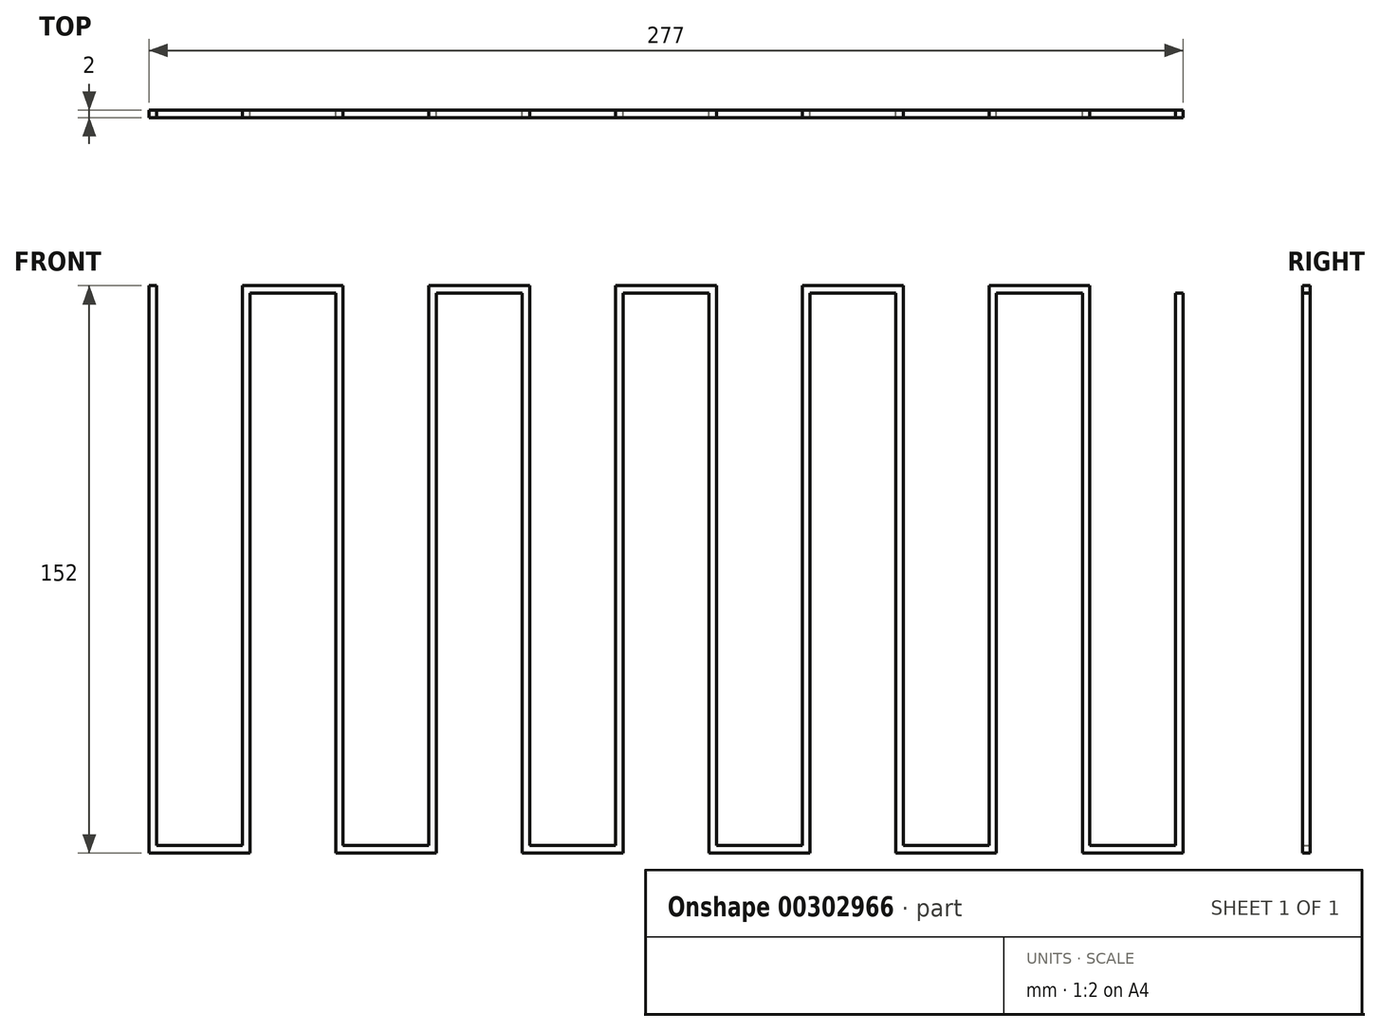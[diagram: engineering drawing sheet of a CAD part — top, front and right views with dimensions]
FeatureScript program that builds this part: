
annotation { "Feature Type Name" : "Feature", "Feature Type Description" : "" }
export const myFeature = defineFeature(function(context is Context, id is Id, definition is map)
    precondition{}
    {
        {
            var Q0;
            Q0=qCreatedBy(makeId("Front.planeOp"),FACE);
            var sketch = newSketch(context, id + "F0", { "sketchPlane" : qUnion([Q0])});
            skLineSegment(sketch, "E0.bottom", {"start": v(-47.26, 125.58) * mm, "end": v(-45.26, 125.58) * mm});
            skLineSegment(sketch, "E0.top", {"start": v(-47.26, -24.42) * mm, "end": v(-45.26, -24.42) * mm});
            skLineSegment(sketch, "E0.left", {"start": v(-47.26, 125.58) * mm, "end": v(-47.26, -24.42) * mm});
            skLineSegment(sketch, "E0.right", {"start": v(-45.26, 125.58) * mm, "end": v(-45.26, -24.42) * mm});
            skLineSegment(sketch, "E1.bottom", {"start": v(-47.26, -24.42) * mm, "end": v(-22.26, -24.42) * mm});
            skLineSegment(sketch, "E1.top", {"start": v(-47.26, -26.42) * mm, "end": v(-22.26, -26.42) * mm});
            skLineSegment(sketch, "E1.left", {"start": v(-47.26, -24.42) * mm, "end": v(-47.26, -26.42) * mm});
            skLineSegment(sketch, "E1.right", {"start": v(-22.26, -24.42) * mm, "end": v(-22.26, -26.42) * mm});
            skLineSegment(sketch, "E2.bottom", {"start": v(-22.26, -26.42) * mm, "end": v(-20.26, -26.42) * mm});
            skLineSegment(sketch, "E2.top", {"start": v(-22.26, 123.58) * mm, "end": v(-20.26, 123.58) * mm});
            skLineSegment(sketch, "E2.left", {"start": v(-22.26, -26.42) * mm, "end": v(-22.26, 123.58) * mm});
            skLineSegment(sketch, "E2.right", {"start": v(-20.26, -26.42) * mm, "end": v(-20.26, 123.58) * mm});
            skLineSegment(sketch, "E3.bottom", {"start": v(-22.26, 123.58) * mm, "end": v(2.74, 123.58) * mm});
            skLineSegment(sketch, "E3.top", {"start": v(-22.26, 125.58) * mm, "end": v(2.74, 125.58) * mm});
            skLineSegment(sketch, "E3.left", {"start": v(-22.26, 123.58) * mm, "end": v(-22.26, 125.58) * mm});
            skLineSegment(sketch, "E3.right", {"start": v(2.74, 123.58) * mm, "end": v(2.74, 125.58) * mm});
            skLineSegment(sketch, "E4.1.0.0", {"start": v(4.74, 125.58) * mm, "end": v(4.74, -24.42) * mm});
            skLineSegment(sketch, "E4.1.0.1", {"start": v(2.74, -26.42) * mm, "end": v(27.74, -26.42) * mm});
            skLineSegment(sketch, "E4.1.0.2", {"start": v(2.74, -24.42) * mm, "end": v(27.74, -24.42) * mm});
            skLineSegment(sketch, "E4.1.0.3", {"start": v(29.74, -26.42) * mm, "end": v(29.74, 123.58) * mm});
            skLineSegment(sketch, "E4.1.0.4", {"start": v(27.74, 123.58) * mm, "end": v(52.74, 123.58) * mm});
            skLineSegment(sketch, "E4.1.0.5", {"start": v(27.74, -26.42) * mm, "end": v(27.74, 123.58) * mm});
            skLineSegment(sketch, "E4.1.0.6", {"start": v(2.74, 125.58) * mm, "end": v(2.74, -24.42) * mm});
            skLineSegment(sketch, "E4.1.0.7", {"start": v(27.74, 125.58) * mm, "end": v(52.74, 125.58) * mm});
            skLineSegment(sketch, "E4.1.0.8", {"start": v(2.74, 125.58) * mm, "end": v(4.74, 125.58) * mm});
            skLineSegment(sketch, "E4.1.0.9", {"start": v(2.74, -24.42) * mm, "end": v(2.74, -26.42) * mm});
            skLineSegment(sketch, "E4.1.0.10", {"start": v(27.74, -24.42) * mm, "end": v(27.74, -26.42) * mm});
            skLineSegment(sketch, "E4.1.0.11", {"start": v(52.74, 123.58) * mm, "end": v(52.74, 125.58) * mm});
            skLineSegment(sketch, "E4.1.0.12", {"start": v(2.74, -24.42) * mm, "end": v(4.74, -24.42) * mm});
            skLineSegment(sketch, "E4.1.0.13", {"start": v(27.74, -26.42) * mm, "end": v(29.74, -26.42) * mm});
            skLineSegment(sketch, "E4.1.0.14", {"start": v(27.74, 123.58) * mm, "end": v(29.74, 123.58) * mm});
            skLineSegment(sketch, "E4.1.0.15", {"start": v(27.74, 123.58) * mm, "end": v(27.74, 125.58) * mm});
            skLineSegment(sketch, "E4.2.0.0", {"start": v(54.74, 125.58) * mm, "end": v(54.74, -24.42) * mm});
            skLineSegment(sketch, "E4.2.0.1", {"start": v(52.74, -26.42) * mm, "end": v(77.74, -26.42) * mm});
            skLineSegment(sketch, "E4.2.0.2", {"start": v(52.74, -24.42) * mm, "end": v(77.74, -24.42) * mm});
            skLineSegment(sketch, "E4.2.0.3", {"start": v(79.74, -26.42) * mm, "end": v(79.74, 123.58) * mm});
            skLineSegment(sketch, "E4.2.0.4", {"start": v(77.74, 123.58) * mm, "end": v(102.74, 123.58) * mm});
            skLineSegment(sketch, "E4.2.0.5", {"start": v(77.74, -26.42) * mm, "end": v(77.74, 123.58) * mm});
            skLineSegment(sketch, "E4.2.0.6", {"start": v(52.74, 125.58) * mm, "end": v(52.74, -24.42) * mm});
            skLineSegment(sketch, "E4.2.0.7", {"start": v(77.74, 125.58) * mm, "end": v(102.74, 125.58) * mm});
            skLineSegment(sketch, "E4.2.0.8", {"start": v(52.74, 125.58) * mm, "end": v(54.74, 125.58) * mm});
            skLineSegment(sketch, "E4.2.0.9", {"start": v(52.74, -24.42) * mm, "end": v(52.74, -26.42) * mm});
            skLineSegment(sketch, "E4.2.0.10", {"start": v(77.74, -24.42) * mm, "end": v(77.74, -26.42) * mm});
            skLineSegment(sketch, "E4.2.0.11", {"start": v(102.74, 123.58) * mm, "end": v(102.74, 125.58) * mm});
            skLineSegment(sketch, "E4.2.0.12", {"start": v(52.74, -24.42) * mm, "end": v(54.74, -24.42) * mm});
            skLineSegment(sketch, "E4.2.0.13", {"start": v(77.74, -26.42) * mm, "end": v(79.74, -26.42) * mm});
            skLineSegment(sketch, "E4.2.0.14", {"start": v(77.74, 123.58) * mm, "end": v(79.74, 123.58) * mm});
            skLineSegment(sketch, "E4.2.0.15", {"start": v(77.74, 123.58) * mm, "end": v(77.74, 125.58) * mm});
            skLineSegment(sketch, "E4.3.0.0", {"start": v(104.74, 125.58) * mm, "end": v(104.74, -24.42) * mm});
            skLineSegment(sketch, "E4.3.0.1", {"start": v(102.74, -26.42) * mm, "end": v(127.74, -26.42) * mm});
            skLineSegment(sketch, "E4.3.0.2", {"start": v(102.74, -24.42) * mm, "end": v(127.74, -24.42) * mm});
            skLineSegment(sketch, "E4.3.0.3", {"start": v(129.74, -26.42) * mm, "end": v(129.74, 123.58) * mm});
            skLineSegment(sketch, "E4.3.0.4", {"start": v(127.74, 123.58) * mm, "end": v(152.74, 123.58) * mm});
            skLineSegment(sketch, "E4.3.0.5", {"start": v(127.74, -26.42) * mm, "end": v(127.74, 123.58) * mm});
            skLineSegment(sketch, "E4.3.0.6", {"start": v(102.74, 125.58) * mm, "end": v(102.74, -24.42) * mm});
            skLineSegment(sketch, "E4.3.0.7", {"start": v(127.74, 125.58) * mm, "end": v(152.74, 125.58) * mm});
            skLineSegment(sketch, "E4.3.0.8", {"start": v(102.74, 125.58) * mm, "end": v(104.74, 125.58) * mm});
            skLineSegment(sketch, "E4.3.0.9", {"start": v(102.74, -24.42) * mm, "end": v(102.74, -26.42) * mm});
            skLineSegment(sketch, "E4.3.0.10", {"start": v(127.74, -24.42) * mm, "end": v(127.74, -26.42) * mm});
            skLineSegment(sketch, "E4.3.0.11", {"start": v(152.74, 123.58) * mm, "end": v(152.74, 125.58) * mm});
            skLineSegment(sketch, "E4.3.0.12", {"start": v(102.74, -24.42) * mm, "end": v(104.74, -24.42) * mm});
            skLineSegment(sketch, "E4.3.0.13", {"start": v(127.74, -26.42) * mm, "end": v(129.74, -26.42) * mm});
            skLineSegment(sketch, "E4.3.0.14", {"start": v(127.74, 123.58) * mm, "end": v(129.74, 123.58) * mm});
            skLineSegment(sketch, "E4.3.0.15", {"start": v(127.74, 123.58) * mm, "end": v(127.74, 125.58) * mm});
            skLineSegment(sketch, "E4.4.0.0", {"start": v(154.74, 125.58) * mm, "end": v(154.74, -24.42) * mm});
            skLineSegment(sketch, "E4.4.0.1", {"start": v(152.74, -26.42) * mm, "end": v(177.74, -26.42) * mm});
            skLineSegment(sketch, "E4.4.0.2", {"start": v(152.74, -24.42) * mm, "end": v(177.74, -24.42) * mm});
            skLineSegment(sketch, "E4.4.0.3", {"start": v(179.74, -26.42) * mm, "end": v(179.74, 123.58) * mm});
            skLineSegment(sketch, "E4.4.0.4", {"start": v(177.74, 123.58) * mm, "end": v(202.74, 123.58) * mm});
            skLineSegment(sketch, "E4.4.0.5", {"start": v(177.74, -26.42) * mm, "end": v(177.74, 123.58) * mm});
            skLineSegment(sketch, "E4.4.0.6", {"start": v(152.74, 125.58) * mm, "end": v(152.74, -24.42) * mm});
            skLineSegment(sketch, "E4.4.0.7", {"start": v(177.74, 125.58) * mm, "end": v(202.74, 125.58) * mm});
            skLineSegment(sketch, "E4.4.0.8", {"start": v(152.74, 125.58) * mm, "end": v(154.74, 125.58) * mm});
            skLineSegment(sketch, "E4.4.0.9", {"start": v(152.74, -24.42) * mm, "end": v(152.74, -26.42) * mm});
            skLineSegment(sketch, "E4.4.0.10", {"start": v(177.74, -24.42) * mm, "end": v(177.74, -26.42) * mm});
            skLineSegment(sketch, "E4.4.0.11", {"start": v(202.74, 123.58) * mm, "end": v(202.74, 125.58) * mm});
            skLineSegment(sketch, "E4.4.0.12", {"start": v(152.74, -24.42) * mm, "end": v(154.74, -24.42) * mm});
            skLineSegment(sketch, "E4.4.0.13", {"start": v(177.74, -26.42) * mm, "end": v(179.74, -26.42) * mm});
            skLineSegment(sketch, "E4.4.0.14", {"start": v(177.74, 123.58) * mm, "end": v(179.74, 123.58) * mm});
            skLineSegment(sketch, "E4.4.0.15", {"start": v(177.74, 123.58) * mm, "end": v(177.74, 125.58) * mm});
            skLineSegment(sketch, "E4.5.0.0", {"start": v(204.74, 125.58) * mm, "end": v(204.74, -24.42) * mm});
            skLineSegment(sketch, "E4.5.0.1", {"start": v(202.74, -26.42) * mm, "end": v(227.74, -26.42) * mm});
            skLineSegment(sketch, "E4.5.0.2", {"start": v(202.74, -24.42) * mm, "end": v(227.74, -24.42) * mm});
            skLineSegment(sketch, "E4.5.0.3", {"start": v(229.74, -26.42) * mm, "end": v(229.74, 123.58) * mm});
            skLineSegment(sketch, "E4.5.0.5", {"start": v(227.74, -26.42) * mm, "end": v(227.74, 123.58) * mm});
            skLineSegment(sketch, "E4.5.0.6", {"start": v(202.74, 125.58) * mm, "end": v(202.74, -24.42) * mm});
            skLineSegment(sketch, "E4.5.0.8", {"start": v(202.74, 125.58) * mm, "end": v(204.74, 125.58) * mm});
            skLineSegment(sketch, "E4.5.0.9", {"start": v(202.74, -24.42) * mm, "end": v(202.74, -26.42) * mm});
            skLineSegment(sketch, "E4.5.0.10", {"start": v(227.74, -24.42) * mm, "end": v(227.74, -26.42) * mm});
            skLineSegment(sketch, "E4.5.0.12", {"start": v(202.74, -24.42) * mm, "end": v(204.74, -24.42) * mm});
            skLineSegment(sketch, "E4.5.0.13", {"start": v(227.74, -26.42) * mm, "end": v(229.74, -26.42) * mm});
            skLineSegment(sketch, "E4.5.0.14", {"start": v(227.74, 123.58) * mm, "end": v(229.74, 123.58) * mm});
            skLineSegment(sketch, "E4.5.0.15", {"start": v(227.74, 123.58) * mm, "end": v(227.74, 125.58) * mm});
            skLineSegment(sketch, "E4.direction1", {"start": v(-47.26, -26.42) * mm, "end": v(2.74, -26.42) * mm, "construction": true});
            skSolve(sketch);
        }
        {
            var Q0;
            {var subQ9=sQuery(id+"F0.wireOp",EDGE,"E4.5.0.1");var subQ11=sQuery(id+"F0.wireOp",EDGE,"E4.4.0.11");var subQ12=makeQuery(id+"F0.imprint","IMPRINT",EDGE,{"derivedFrom":subQ11});var subQ14=sQuery(id+"F0.wireOp",EDGE,"E4.4.0.3");var subQ21=sQuery(id+"F0.wireOp",EDGE,"E4.4.0.1");var subQ30=sQuery(id+"F0.wireOp",EDGE,"E4.3.0.11");var subQ31=makeQuery(id+"F0.imprint","IMPRINT",EDGE,{"derivedFrom":subQ30});var subQ33=sQuery(id+"F0.wireOp",EDGE,"E4.3.0.3");var subQ40=sQuery(id+"F0.wireOp",EDGE,"E4.3.0.1");var subQ49=sQuery(id+"F0.wireOp",EDGE,"E4.2.0.11");var subQ50=makeQuery(id+"F0.imprint","IMPRINT",EDGE,{"derivedFrom":subQ49});var subQ52=sQuery(id+"F0.wireOp",EDGE,"E4.2.0.3");var subQ59=sQuery(id+"F0.wireOp",EDGE,"E4.2.0.1");var subQ68=sQuery(id+"F0.wireOp",EDGE,"E4.1.0.11");var subQ69=makeQuery(id+"F0.imprint","IMPRINT",EDGE,{"derivedFrom":subQ68});var subQ71=sQuery(id+"F0.wireOp",EDGE,"E4.1.0.3");var subQ78=sQuery(id+"F0.wireOp",EDGE,"E4.1.0.1");var subQ87=makeQuery(id+"F0.imprint","IMPRINT",EDGE,{"derivedFrom":sQuery(id+"F0.wireOp",EDGE,"E3.right")});var subQ88=makeQuery(id+"F0.imprint","IMPRINT",EDGE,{"derivedFrom":sQuery(id+"F0.wireOp",EDGE,"E2.top")});var subQ89=makeQuery(id+"F0.imprint","IMPRINT",EDGE,{"derivedFrom":sQuery(id+"F0.wireOp",EDGE,"E1.right")});var subQ90=makeQuery(id+"F0.imprint","IMPRINT",EDGE,{"derivedFrom":sQuery(id+"F0.wireOp",EDGE,"E0.top")});Q0=qUnion([makeQuery(id+"F0.imprint","IMPRINT",FACE,{"disambiguationData":[TD([[makeQuery(id+"F0.imprint","IMPRINT",EDGE,{"derivedFrom":sQuery(id+"F0.wireOp",EDGE,"E0.bottom")}),-1.0]])]}),makeQuery(id+"F0.imprint","IMPRINT",FACE,{"disambiguationData":[TD([[makeQuery(id+"F0.imprint","IMPRINT",EDGE,{"derivedFrom":sQuery(id+"F0.wireOp",EDGE,"E4.5.0.3")}),1.0]])]}),makeQuery(id+"F0.imprint","IMPRINT",FACE,{"disambiguationData":[TD([[subQ90,-1.0]])]}),makeQuery(id+"F0.imprint","IMPRINT",FACE,{"disambiguationData":[TD([[subQ89,1.0]])]}),makeQuery(id+"F0.imprint","IMPRINT",FACE,{"disambiguationData":[TD([[subQ88,1.0]])]}),makeQuery(id+"F0.imprint","IMPRINT",FACE,{"disambiguationData":[TD([[subQ87,-1.0]])]}),makeQuery(id+"F0.imprint","IMPRINT",FACE,{"disambiguationData":[TD([[makeQuery(id+"F0.imprint","IMPRINT",EDGE,{"derivedFrom":subQ78}),1.0]])]}),makeQuery(id+"F0.imprint","IMPRINT",FACE,{"disambiguationData":[TD([[makeQuery(id+"F0.imprint","IMPRINT",EDGE,{"derivedFrom":subQ71}),1.0]])]}),makeQuery(id+"F0.imprint","IMPRINT",FACE,{"disambiguationData":[TD([[makeQuery(id+"F0.imprint","IMPRINT",EDGE,{"derivedFrom":sQuery(id+"F0.wireOp",EDGE,"E4.1.0.7")}),-1.0]])]}),makeQuery(id+"F0.imprint","IMPRINT",FACE,{"disambiguationData":[TD([[subQ69,-1.0]])]}),makeQuery(id+"F0.imprint","IMPRINT",FACE,{"disambiguationData":[TD([[makeQuery(id+"F0.imprint","IMPRINT",EDGE,{"derivedFrom":subQ59}),1.0]])]}),makeQuery(id+"F0.imprint","IMPRINT",FACE,{"disambiguationData":[TD([[makeQuery(id+"F0.imprint","IMPRINT",EDGE,{"derivedFrom":subQ52}),1.0]])]}),makeQuery(id+"F0.imprint","IMPRINT",FACE,{"disambiguationData":[TD([[makeQuery(id+"F0.imprint","IMPRINT",EDGE,{"derivedFrom":sQuery(id+"F0.wireOp",EDGE,"E4.2.0.7")}),-1.0]])]}),makeQuery(id+"F0.imprint","IMPRINT",FACE,{"disambiguationData":[TD([[subQ50,-1.0]])]}),makeQuery(id+"F0.imprint","IMPRINT",FACE,{"disambiguationData":[TD([[makeQuery(id+"F0.imprint","IMPRINT",EDGE,{"derivedFrom":subQ40}),1.0]])]}),makeQuery(id+"F0.imprint","IMPRINT",FACE,{"disambiguationData":[TD([[makeQuery(id+"F0.imprint","IMPRINT",EDGE,{"derivedFrom":subQ33}),1.0]])]}),makeQuery(id+"F0.imprint","IMPRINT",FACE,{"disambiguationData":[TD([[makeQuery(id+"F0.imprint","IMPRINT",EDGE,{"derivedFrom":sQuery(id+"F0.wireOp",EDGE,"E4.3.0.7")}),-1.0]])]}),makeQuery(id+"F0.imprint","IMPRINT",FACE,{"disambiguationData":[TD([[subQ31,-1.0]])]}),makeQuery(id+"F0.imprint","IMPRINT",FACE,{"disambiguationData":[TD([[makeQuery(id+"F0.imprint","IMPRINT",EDGE,{"derivedFrom":subQ21}),1.0]])]}),makeQuery(id+"F0.imprint","IMPRINT",FACE,{"disambiguationData":[TD([[makeQuery(id+"F0.imprint","IMPRINT",EDGE,{"derivedFrom":subQ14}),1.0]])]}),makeQuery(id+"F0.imprint","IMPRINT",FACE,{"disambiguationData":[TD([[makeQuery(id+"F0.imprint","IMPRINT",EDGE,{"derivedFrom":sQuery(id+"F0.wireOp",EDGE,"E4.4.0.7")}),-1.0]])]}),makeQuery(id+"F0.imprint","IMPRINT",FACE,{"disambiguationData":[TD([[subQ12,-1.0]])]}),makeQuery(id+"F0.imprint","IMPRINT",FACE,{"disambiguationData":[TD([[makeQuery(id+"F0.imprint","IMPRINT",EDGE,{"derivedFrom":subQ9}),1.0]])]})]);}
            extrude(context, id + "F1", {"entities" : qUnion([Q0]), "depth" : 2 * mm, "offsetDistance" : 25 * mm});
        }
    });
